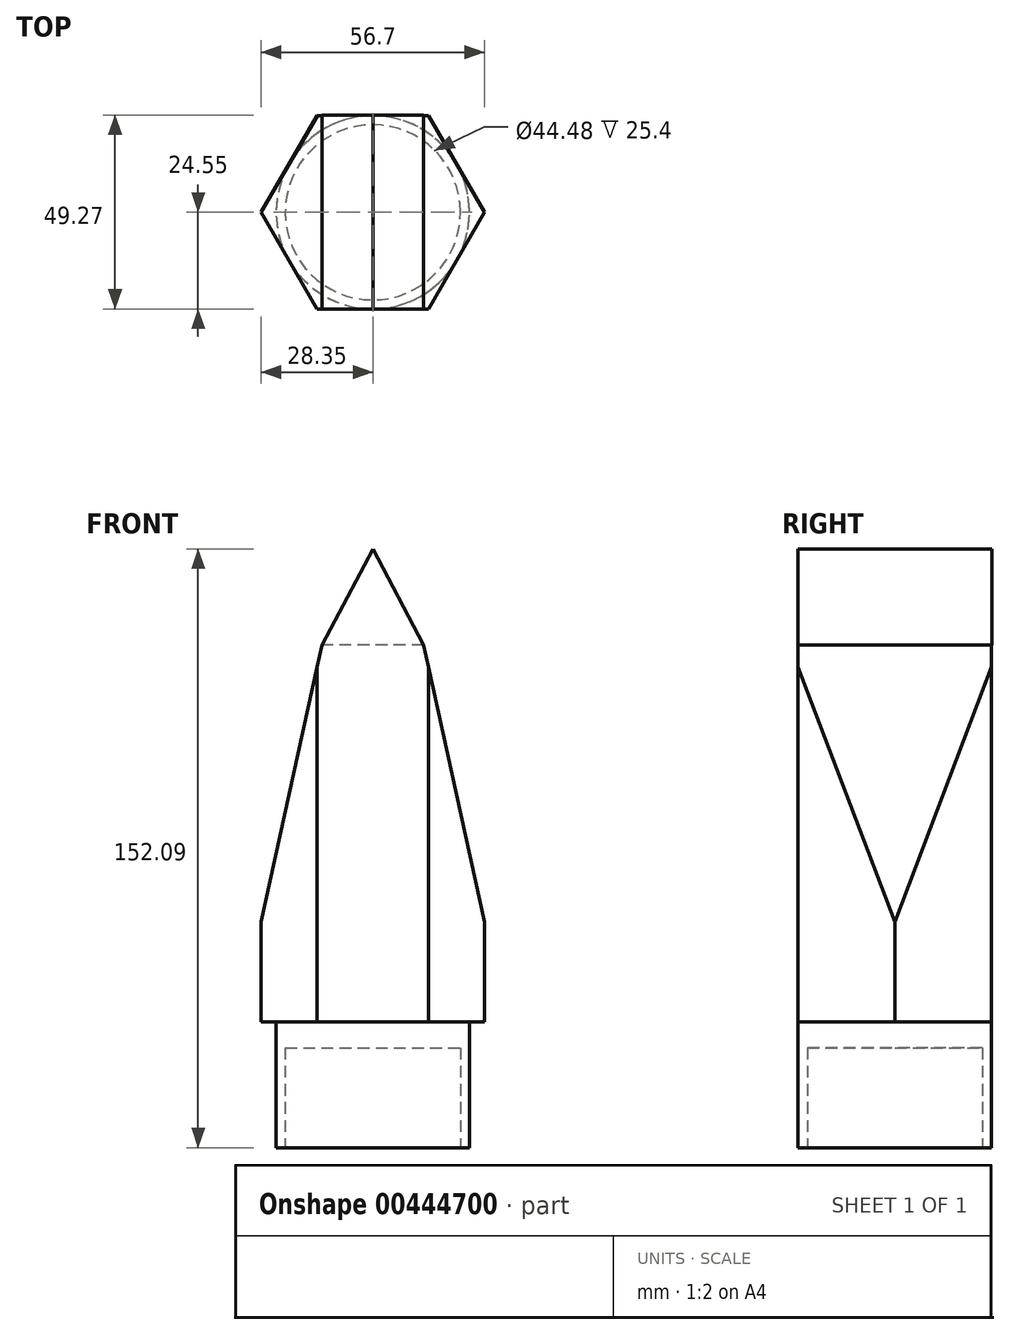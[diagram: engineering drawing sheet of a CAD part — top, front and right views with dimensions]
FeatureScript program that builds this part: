
annotation { "Feature Type Name" : "Feature", "Feature Type Description" : "" }
export const myFeature = defineFeature(function(context is Context, id is Id, definition is map)
    precondition{}
    {
        {
            var Q0;
            Q0=qCreatedBy(makeId("Top.planeOp"),FACE);
            var sketch = newSketch(context, id + "F0", { "sketchPlane" : qUnion([Q0])});
            skCircle(sketch, "E0", {"center": v(0, 0) * mm, "radius": 24.55 * mm});
            skSolve(sketch);
        }
        {
            var Q0;
            Q0=makeQuery(id+"F0.imprint","IMPRINT",FACE,{"disambiguationData":[TD([[makeQuery(id+"F0.imprint","IMPRINT",EDGE,{"derivedFrom":sQuery(id+"F0.wireOp",EDGE,"E0")}),1.0]])]});
            extrude(context, id + "F1", {"entities" : qUnion([Q0]), "depth" : 32 * mm});
        }
        {
            var Q0;
            Q0=makeQuery(id+"F1.opExtrude","CAP_FACE",FACE,{"disambiguationData":[OSD([sQuery(id+"F0.wireOp",EDGE,"E0")])],"isStart":true});
            var sketch = newSketch(context, id + "F2", { "sketchPlane" : qUnion([Q0])});
            skCircle(sketch, "E1", {"center": v(0, 0) * mm, "radius": 22.24 * mm});
            skSolve(sketch);
        }
        {
            var Q0;
            Q0=makeQuery(id+"F2.imprint","IMPRINT",FACE,{"disambiguationData":[TD([[makeQuery(id+"F2.imprint","IMPRINT",EDGE,{"derivedFrom":sQuery(id+"F2.wireOp",EDGE,"E1")}),1.0]])]});
            extrude(context, id + "F3", {"entities" : qUnion([Q0]), "operationType" : NewBodyOperationType.REMOVE, "oppositeDirection" : true, "depth" : 25.4 * mm});
        }
        {
            var Q0;
            Q0=makeQuery(id+"F1.opExtrude","CAP_FACE",FACE,{"disambiguationData":[OSD([sQuery(id+"F0.wireOp",EDGE,"E0")])],"isStart":false});
            var sketch = newSketch(context, id + "F4", { "sketchPlane" : qUnion([Q0])});
            skCircle(sketch, "E2.cCircle", {"center": v(0, 0) * mm, "radius": 24.55 * mm, "construction": true});
            skLineSegment(sketch, "E2.0", {"start": v(-14.18, 24.55) * mm, "end": v(14.18, 24.55) * mm});
            skLineSegment(sketch, "E2.1", {"start": v(14.18, 24.55) * mm, "end": v(28.35, 0) * mm});
            skLineSegment(sketch, "E2.2", {"start": v(28.35, 0) * mm, "end": v(14.18, -24.55) * mm});
            skLineSegment(sketch, "E2.3", {"start": v(14.18, -24.55) * mm, "end": v(-14.18, -24.55) * mm});
            skLineSegment(sketch, "E2.4", {"start": v(-14.18, -24.55) * mm, "end": v(-28.35, 0) * mm});
            skLineSegment(sketch, "E2.5", {"start": v(-28.35, 0) * mm, "end": v(-14.18, 24.55) * mm});
            skPoint(sketch, "E2.0.midPoint", {"position": v(0, 24.55) * mm});
            skSolve(sketch);
        }
        {
            var Q0;
            {var subQ0=sQuery(id+"F4.wireOp",EDGE,"E2.2");var subQ1=sQuery(id+"F4.wireOp",EDGE,"E2.1");var subQ2=makeQuery(id+"F4.imprint","INTERSECT",VERTEX,{"derivedFrom":[subQ1,subQ0]});Q0=makeQuery(id+"F4.imprint","IMPRINT",FACE,{"disambiguationData":[TD([[makeQuery(id+"F4.imprint","IMPRINT",EDGE,{"disambiguationData":[TD([[subQ2,1.0]])],"derivedFrom":subQ1}),-1.0]])]});}
            var Q1;
            {var subQ0=makeQuery(id+"F1.opExtrude","CAP_EDGE",EDGE,{"disambiguationData":[OSD([sQuery(id+"F0.wireOp",EDGE,"E0")])],"isStart":false});var subQ4=makeQuery(id+"F4.imprint","INTERSECT",VERTEX,{"derivedFrom":[subQ0,sQuery(id+"F4.wireOp",EDGE,"E2.0")]});Q1=makeQuery(id+"F4.imprint","IMPRINT",FACE,{"disambiguationData":[TD([[makeQuery(id+"F4.imprint","IMPRINT",EDGE,{"disambiguationData":[TD([[subQ4,1.0]])],"derivedFrom":subQ0}),1.0]])]});}
            var Q2;
            {var subQ0=sQuery(id+"F4.wireOp",EDGE,"E2.5");var subQ1=sQuery(id+"F4.wireOp",EDGE,"E2.4");var subQ2=makeQuery(id+"F4.imprint","INTERSECT",VERTEX,{"derivedFrom":[subQ1,subQ0]});Q2=makeQuery(id+"F4.imprint","IMPRINT",FACE,{"disambiguationData":[TD([[makeQuery(id+"F4.imprint","IMPRINT",EDGE,{"disambiguationData":[TD([[subQ2,1.0]])],"derivedFrom":subQ1}),-1.0]])]});}
            var Q3;
            {var subQ0=sQuery(id+"F4.wireOp",EDGE,"E2.5");var subQ1=sQuery(id+"F4.wireOp",EDGE,"E2.0");var subQ2=makeQuery(id+"F4.imprint","INTERSECT",VERTEX,{"derivedFrom":[subQ1,subQ0]});Q3=makeQuery(id+"F4.imprint","IMPRINT",FACE,{"disambiguationData":[TD([[makeQuery(id+"F4.imprint","IMPRINT",EDGE,{"disambiguationData":[TD([[subQ2,-1.0]])],"derivedFrom":subQ1}),-1.0]])]});}
            var Q4;
            {var subQ0=sQuery(id+"F4.wireOp",EDGE,"E2.1");var subQ1=sQuery(id+"F4.wireOp",EDGE,"E2.0");var subQ2=makeQuery(id+"F4.imprint","INTERSECT",VERTEX,{"derivedFrom":[subQ1,subQ0]});Q4=makeQuery(id+"F4.imprint","IMPRINT",FACE,{"disambiguationData":[TD([[makeQuery(id+"F4.imprint","IMPRINT",EDGE,{"disambiguationData":[TD([[subQ2,1.0]])],"derivedFrom":subQ1}),-1.0]])]});}
            var Q5;
            {var subQ0=sQuery(id+"F4.wireOp",EDGE,"E2.4");var subQ1=sQuery(id+"F4.wireOp",EDGE,"E2.3");var subQ2=makeQuery(id+"F4.imprint","INTERSECT",VERTEX,{"derivedFrom":[subQ1,subQ0]});Q5=makeQuery(id+"F4.imprint","IMPRINT",FACE,{"disambiguationData":[TD([[makeQuery(id+"F4.imprint","IMPRINT",EDGE,{"disambiguationData":[TD([[subQ2,1.0]])],"derivedFrom":subQ1}),-1.0]])]});}
            var Q6;
            {var subQ0=sQuery(id+"F4.wireOp",EDGE,"E2.3");var subQ1=sQuery(id+"F4.wireOp",EDGE,"E2.2");var subQ2=makeQuery(id+"F4.imprint","INTERSECT",VERTEX,{"derivedFrom":[subQ1,subQ0]});Q6=makeQuery(id+"F4.imprint","IMPRINT",FACE,{"disambiguationData":[TD([[makeQuery(id+"F4.imprint","IMPRINT",EDGE,{"disambiguationData":[TD([[subQ2,1.0]])],"derivedFrom":subQ1}),-1.0]])]});}
            extrude(context, id + "F5", {"entities" : qUnion([Q0, Q1, Q2, Q3, Q4, Q5, Q6]), "operationType" : NewBodyOperationType.ADD, "depth" : 25.4 * mm});
        }
        {
            var Q0;
            Q0=qCreatedBy(makeId("Front.planeOp"),FACE);
            var sketch = newSketch(context, id + "F6", { "sketchPlane" : qUnion([Q0])});
            skLineSegment(sketch, "E3", {"start": v(28.35, 57.4) * mm, "end": v(12.93, 127.77) * mm});
            skLineSegment(sketch, "E4", {"start": v(12.93, 127.77) * mm, "end": v(-12.93, 127.77) * mm});
            skLineSegment(sketch, "E5", {"start": v(-12.93, 127.77) * mm, "end": v(-28.35, 57.4) * mm});
            skLineSegment(sketch, "E6", {"start": v(-28.35, 57.4) * mm, "end": v(28.35, 57.4) * mm});
            skSolve(sketch);
        }
        {
            var Q0;
            Q0 = qSketchRegion(id + "F6", true);
            var Q1;
            Q1=makeQuery(id+"F5.opExtrude","SWEPT_FACE",FACE,{"disambiguationData":[OSD([sQuery(id+"F4.wireOp",EDGE,"E2.0")])]});
            var Q2;
            Q2=makeQuery(id+"F5.opExtrude","SWEPT_FACE",FACE,{"disambiguationData":[OSD([sQuery(id+"F4.wireOp",EDGE,"E2.3")])]});
            extrude(context, id + "F7", {"entities" : qUnion([Q0]), "operationType" : NewBodyOperationType.ADD, "endBound" : BoundingType.UP_TO_SURFACE, "oppositeDirection" : true, "endBoundEntityFace" : qUnion([Q1]), "depth" : 25.4 * mm, "hasSecondDirection" : true, "secondDirectionBound" : SecondDirectionBoundingType.UP_TO_SURFACE, "secondDirectionOppositeDirection" : false, "secondDirectionBoundEntityFace" : qUnion([Q2]), "secondDirectionDepth" : 22.1 * mm});
        }
        {
            var Q0;
            {var subQ0=sQuery(id+"F4.wireOp",EDGE,"E2.3");var subQ1=makeQuery(id+"F7.opExtrude","SWEPT_FACE",FACE,{"disambiguationData":[OSD([sQuery(id+"F6.wireOp",EDGE,"E6")])]});Q0=makeQuery(id+"F7.boolean.opBoolean","SPLIT",FACE,{"disambiguationData":[TD([makeQuery(id+"F5.opExtrude","SWEPT_FACE",FACE,{"disambiguationData":[OSD([sQuery(id+"F4.wireOp",EDGE,"E2.1")])]}),makeQuery(id+"F5.opExtrude","SWEPT_FACE",FACE,{"disambiguationData":[OSD([sQuery(id+"F4.wireOp",EDGE,"E2.2")])]}),makeQuery(id+"F5.opExtrude","SWEPT_FACE",FACE,{"disambiguationData":[OSD([subQ0])]}),makeQuery(id+"F7.opExtrude","CAP_FACE",FACE,{"disambiguationData":[OSD([subQ0])],"isStart":true}),makeQuery(id+"F7.opExtrude","SWEPT_FACE",FACE,{"disambiguationData":[OSD([sQuery(id+"F6.wireOp",EDGE,"E3")])]}),subQ1])],"derivedFrom":subQ1});}
            var sketch = newSketch(context, id + "F8", { "sketchPlane" : qUnion([Q0])});
            skLineSegment(sketch, "E7", {"start": v(14.18, 24.55) * mm, "end": v(28.35, 0) * mm});
            skLineSegment(sketch, "E8", {"start": v(28.35, 0) * mm, "end": v(28.35, 24.55) * mm});
            skLineSegment(sketch, "E9", {"start": v(28.35, 24.55) * mm, "end": v(14.18, 24.55) * mm});
            skSolve(sketch);
        }
        {
            var Q0;
            Q0=makeQuery(id+"F8.imprint","IMPRINT",FACE,{"disambiguationData":[TD([[makeQuery(id+"F8.imprint","IMPRINT",EDGE,{"derivedFrom":sQuery(id+"F8.wireOp",EDGE,"E7")}),-1.0]])]});
            extrude(context, id + "F9", {"entities" : qUnion([Q0]), "operationType" : NewBodyOperationType.REMOVE, "oppositeDirection" : true, "depth" : 101.6 * mm, "hasDraft" : true, "draftAngle" : 0 * degree});
        }
        {
            var Q0;
            {var subQ0=sQuery(id+"F4.wireOp",EDGE,"E2.0");var subQ1=makeQuery(id+"F7.opExtrude","SWEPT_FACE",FACE,{"disambiguationData":[OSD([sQuery(id+"F6.wireOp",EDGE,"E6")])]});Q0=makeQuery(id+"F7.boolean.opBoolean","SPLIT",FACE,{"disambiguationData":[TD([makeQuery(id+"F5.opExtrude","SWEPT_FACE",FACE,{"disambiguationData":[OSD([subQ0])]}),makeQuery(id+"F5.opExtrude","SWEPT_FACE",FACE,{"disambiguationData":[OSD([sQuery(id+"F4.wireOp",EDGE,"E2.1")])]}),makeQuery(id+"F5.opExtrude","SWEPT_FACE",FACE,{"disambiguationData":[OSD([sQuery(id+"F4.wireOp",EDGE,"E2.2")])]}),makeQuery(id+"F7.opExtrude","CAP_FACE",FACE,{"disambiguationData":[OSD([subQ0])],"isStart":false}),makeQuery(id+"F7.opExtrude","SWEPT_FACE",FACE,{"disambiguationData":[OSD([sQuery(id+"F6.wireOp",EDGE,"E3")])]}),subQ1])],"derivedFrom":subQ1});}
            var sketch = newSketch(context, id + "F10", { "sketchPlane" : qUnion([Q0])});
            skLineSegment(sketch, "E10", {"start": v(28.35, 0) * mm, "end": v(28.35, -24.55) * mm});
            skLineSegment(sketch, "E11", {"start": v(28.35, -24.55) * mm, "end": v(14.18, -24.55) * mm});
            skLineSegment(sketch, "E12", {"start": v(14.18, -24.55) * mm, "end": v(28.35, 0) * mm});
            skSolve(sketch);
        }
        {
            var Q0;
            Q0=makeQuery(id+"F10.imprint","IMPRINT",FACE,{"disambiguationData":[TD([[makeQuery(id+"F10.imprint","IMPRINT",EDGE,{"derivedFrom":sQuery(id+"F10.wireOp",EDGE,"E10")}),1.0]])]});
            extrude(context, id + "F11", {"entities" : qUnion([Q0]), "operationType" : NewBodyOperationType.REMOVE, "oppositeDirection" : true, "depth" : 84.07 * mm, "hasDraft" : true, "draftAngle" : 0 * degree});
        }
        {
            var Q0;
            {var subQ0=sQuery(id+"F4.wireOp",EDGE,"E2.3");var subQ1=makeQuery(id+"F7.opExtrude","SWEPT_FACE",FACE,{"disambiguationData":[OSD([sQuery(id+"F6.wireOp",EDGE,"E6")])]});Q0=makeQuery(id+"F7.boolean.opBoolean","SPLIT",FACE,{"disambiguationData":[TD([makeQuery(id+"F5.opExtrude","SWEPT_FACE",FACE,{"disambiguationData":[OSD([subQ0])]}),makeQuery(id+"F5.opExtrude","SWEPT_FACE",FACE,{"disambiguationData":[OSD([sQuery(id+"F4.wireOp",EDGE,"E2.4")])]}),makeQuery(id+"F5.opExtrude","SWEPT_FACE",FACE,{"disambiguationData":[OSD([sQuery(id+"F4.wireOp",EDGE,"E2.5")])]}),makeQuery(id+"F7.opExtrude","CAP_FACE",FACE,{"disambiguationData":[OSD([subQ0])],"isStart":true}),makeQuery(id+"F7.opExtrude","SWEPT_FACE",FACE,{"disambiguationData":[OSD([sQuery(id+"F6.wireOp",EDGE,"E5")])]}),subQ1])],"derivedFrom":subQ1});}
            extrude(context, id + "F12", {"entities" : qUnion([Q0]), "operationType" : NewBodyOperationType.REMOVE, "oppositeDirection" : true, "depth" : 76.45 * mm, "hasDraft" : true, "draftAngle" : 0 * degree});
        }
        {
            var Q0;
            {var subQ0=sQuery(id+"F4.wireOp",EDGE,"E2.0");var subQ1=makeQuery(id+"F7.opExtrude","SWEPT_FACE",FACE,{"disambiguationData":[OSD([sQuery(id+"F6.wireOp",EDGE,"E6")])]});Q0=makeQuery(id+"F7.boolean.opBoolean","SPLIT",FACE,{"disambiguationData":[TD([makeQuery(id+"F5.opExtrude","SWEPT_FACE",FACE,{"disambiguationData":[OSD([subQ0])]}),makeQuery(id+"F5.opExtrude","SWEPT_FACE",FACE,{"disambiguationData":[OSD([sQuery(id+"F4.wireOp",EDGE,"E2.4")])]}),makeQuery(id+"F5.opExtrude","SWEPT_FACE",FACE,{"disambiguationData":[OSD([sQuery(id+"F4.wireOp",EDGE,"E2.5")])]}),makeQuery(id+"F7.opExtrude","CAP_FACE",FACE,{"disambiguationData":[OSD([subQ0])],"isStart":false}),makeQuery(id+"F7.opExtrude","SWEPT_FACE",FACE,{"disambiguationData":[OSD([sQuery(id+"F6.wireOp",EDGE,"E5")])]}),subQ1])],"derivedFrom":subQ1});}
            extrude(context, id + "F13", {"entities" : qUnion([Q0]), "operationType" : NewBodyOperationType.REMOVE, "oppositeDirection" : true, "depth" : 91.19 * mm, "hasDraft" : true, "draftAngle" : .1 * degree, "hasSecondDirection" : true, "secondDirectionOppositeDirection" : false, "secondDirectionDepth" : 25.4 * mm});
        }
        {
            var Q0;
            {var subQ0=sQuery(id+"F4.wireOp",EDGE,"E2.3");Q0=makeQuery(id+"F7.boolean.opBoolean","MERGE",FACE,{"derivedFrom":[makeQuery(id+"F5.opExtrude","SWEPT_FACE",FACE,{"disambiguationData":[OSD([subQ0])]}),makeQuery(id+"F7.opExtrude","CAP_FACE",FACE,{"disambiguationData":[OSD([subQ0])],"isStart":true})]});}
            var sketch = newSketch(context, id + "F14", { "sketchPlane" : qUnion([Q0])});
            skLineSegment(sketch, "E13", {"start": v(-12.93, 127.77) * mm, "end": v(0, 152.09) * mm});
            skLineSegment(sketch, "E14", {"start": v(0, 152.09) * mm, "end": v(12.93, 127.77) * mm});
            skSolve(sketch);
        }
        {
            var Q0;
            Q0 = qSketchRegion(id + "F14", true);
            var Q1;
            Q1=makeQuery(id+"F14.imprint","IMPRINT",FACE,{"disambiguationData":[TD([[makeQuery(id+"F14.imprint","IMPRINT",EDGE,{"derivedFrom":sQuery(id+"F14.wireOp",EDGE,"E13")}),-1.0]])]});
            extrude(context, id + "F15", {"entities" : qUnion([Q0, Q1]), "operationType" : NewBodyOperationType.ADD, "oppositeDirection" : true, "depth" : 49.28 * mm});
        }
    });
